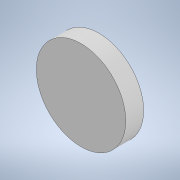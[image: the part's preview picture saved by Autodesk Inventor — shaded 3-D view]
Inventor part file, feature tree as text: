
AUTODESK INVENTOR PART (.ipt)
format: ipt  version: 2021 (Build 250183000, 183)  size: 92,672 bytes
history: native  units: mm
features: other x1, extrude x1, sketch x1
ambient origin geometry x8: Origin, YZ Plane, XZ Plane, XY Plane, X Axis, Y Axis, Z Axis, Center Point
bodies: Body1 (feature_tree)
feature tree (3):
  other  "Sólido1"
  extrude  "Extrusão1"  Depth=1.0mm TaperAngle=0.0deg
  sketch  "Esboço1"  dims[d0=5.0mm d1=1.0mm d2=0.0mm]
